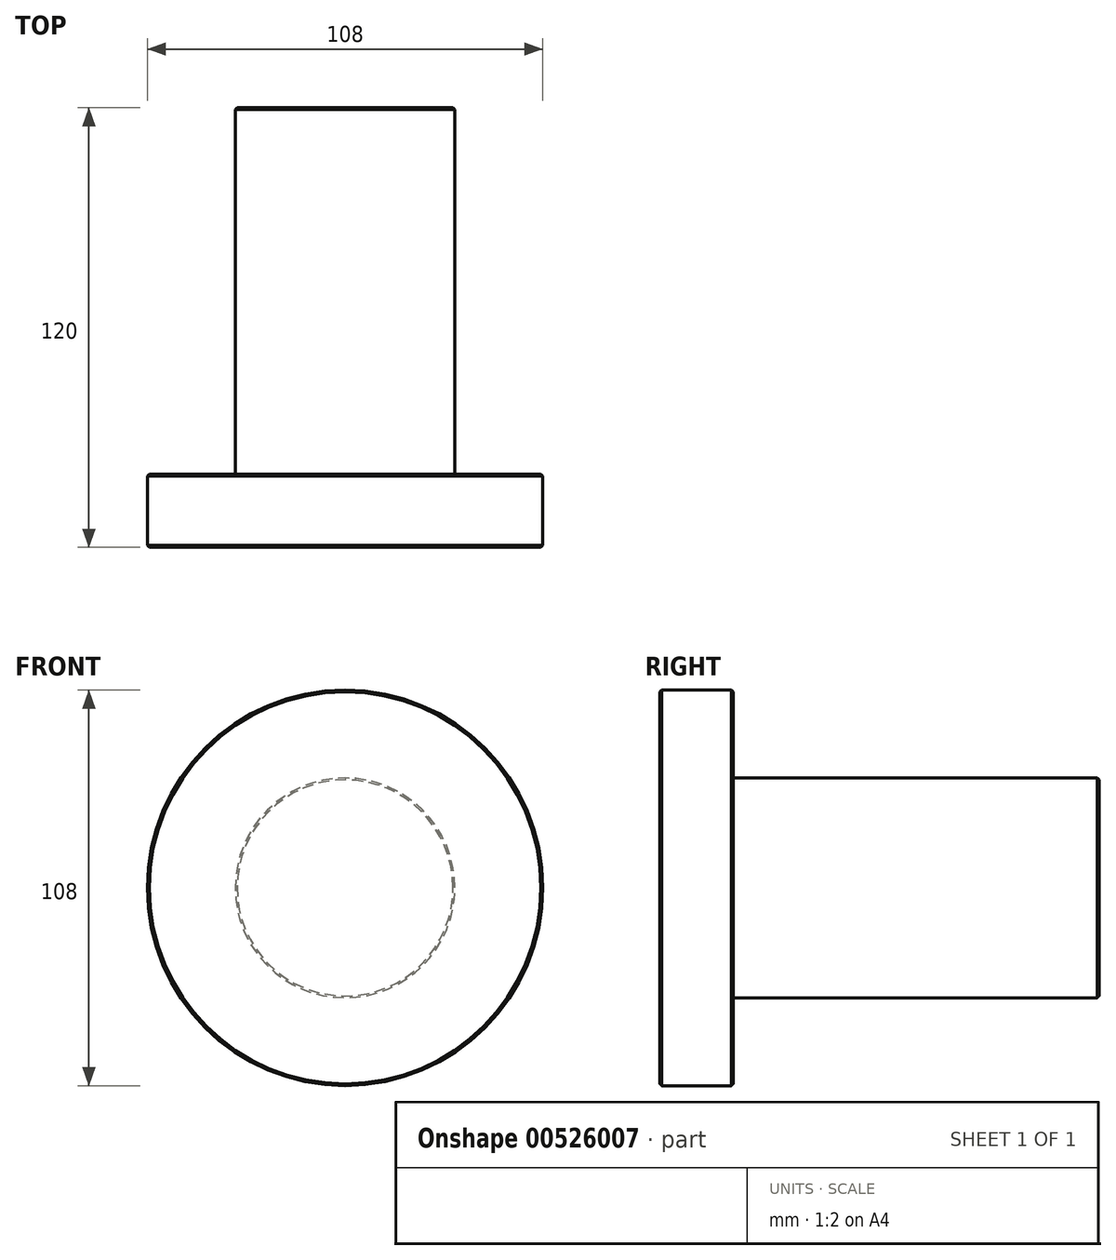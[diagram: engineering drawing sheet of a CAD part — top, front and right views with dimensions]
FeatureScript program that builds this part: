
annotation { "Feature Type Name" : "Feature", "Feature Type Description" : "" }
export const myFeature = defineFeature(function(context is Context, id is Id, definition is map)
    precondition{}
    {
        {
            var Q0;
            Q0=qCreatedBy(makeId("Front.planeOp"),FACE);
            var sketch = newSketch(context, id + "F0", { "sketchPlane" : qUnion([Q0])});
            skCircle(sketch, "E0", {"center": v(0, 0) * mm, "radius": 30 * mm});
            skCircle(sketch, "E1", {"center": v(0, 0) * mm, "radius": 54 * mm});
            skSolve(sketch);
        }
        {
            var Q0;
            Q0=makeQuery(id+"F0.imprint","IMPRINT",FACE,{"disambiguationData":[TD([[makeQuery(id+"F0.imprint","IMPRINT",EDGE,{"derivedFrom":sQuery(id+"F0.wireOp",EDGE,"E0")}),-1.0]])]});
            var Q1;
            Q1=makeQuery(id+"F0.imprint","IMPRINT",FACE,{"disambiguationData":[TD([[makeQuery(id+"F0.imprint","IMPRINT",EDGE,{"derivedFrom":sQuery(id+"F0.wireOp",EDGE,"E0")}),1.0]])]});
            extrude(context, id + "F1", {"entities" : qUnion([Q0, Q1]), "depth" : 20 * mm, "offsetDistance" : 25 * mm});
        }
        {
            var Q0;
            Q0=makeQuery(id+"F0.imprint","IMPRINT",FACE,{"disambiguationData":[TD([[makeQuery(id+"F0.imprint","IMPRINT",EDGE,{"derivedFrom":sQuery(id+"F0.wireOp",EDGE,"E0")}),1.0]])]});
            extrude(context, id + "F2", {"entities" : qUnion([Q0]), "operationType" : NewBodyOperationType.ADD, "oppositeDirection" : true, "depth" : 100 * mm, "offsetDistance" : 25 * mm});
        }
        {
            var Q0;
            Q0=makeQuery(id+"F1.opExtrude","CAP_EDGE",EDGE,{"disambiguationData":[OSD([sQuery(id+"F0.wireOp",EDGE,"E1")])],"isStart":false});
            var Q1;
            Q1=makeQuery(id+"F1.opExtrude","SWEPT_FACE",FACE,{"disambiguationData":[OSD([sQuery(id+"F0.wireOp",EDGE,"E1")])]});
            var Q2;
            Q2=makeQuery(id+"F2.opExtrude","CAP_EDGE",EDGE,{"disambiguationData":[OSD([sQuery(id+"F0.wireOp",EDGE,"E0")])],"isStart":false});
            chamfer(context, id + "F3", {"entities" : qUnion([Q0, Q1, Q2]), "width" : 0.5 * mm, "tangentPropagation" : true});
        }
    });
